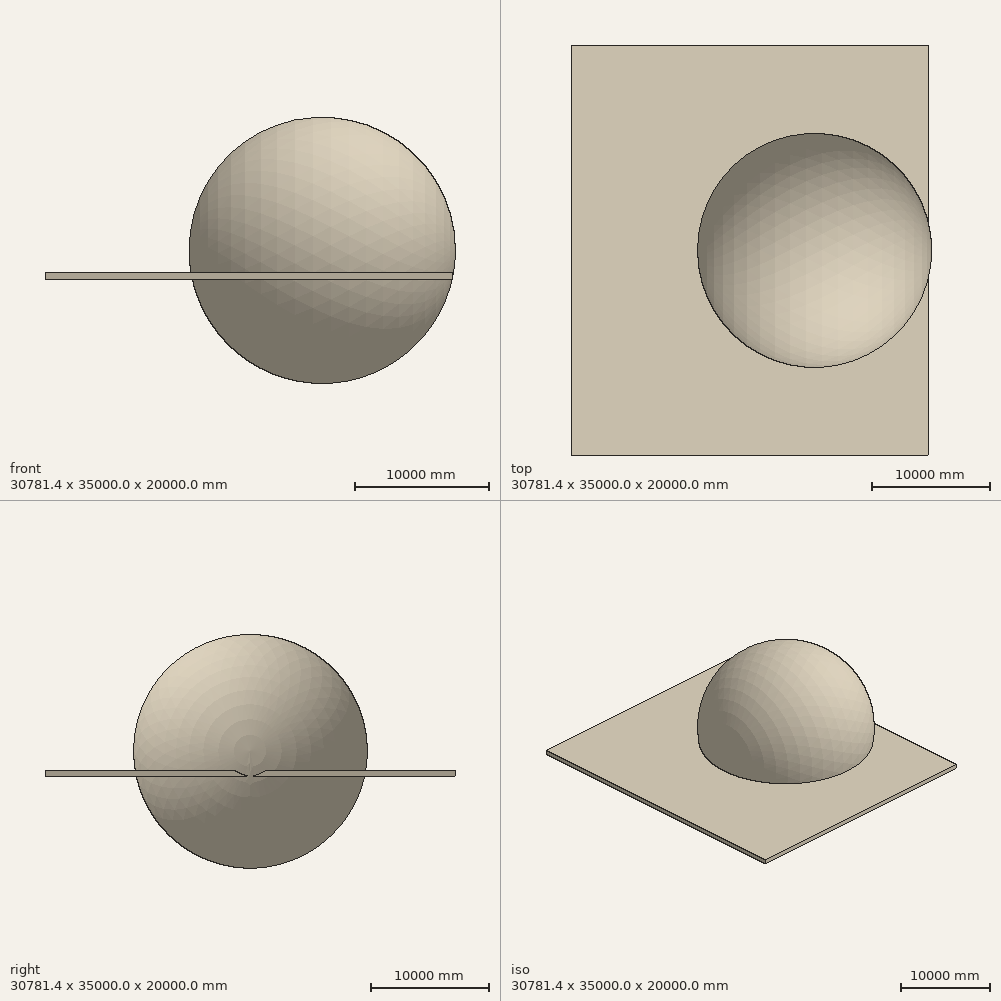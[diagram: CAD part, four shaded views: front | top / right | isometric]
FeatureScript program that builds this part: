
annotation { "Feature Type Name" : "Feature", "Feature Type Description" : "" }
export const myFeature = defineFeature(function(context is Context, id is Id, definition is map)
    precondition{}
    {
        {
            var Q0;
            Q0=qCreatedBy(makeId("Front.planeOp"),FACE);
            var sketch = newSketch(context, id + "F0", { "sketchPlane" : qUnion([Q0])});
            skLineSegment(sketch, "E0.bottom", {"start": v(0, 0) * mm, "end": v(100, 0) * mm});
            skLineSegment(sketch, "E0.top", {"start": v(0, 5000) * mm, "end": v(5000, 5000) * mm});
            skLineSegment(sketch, "E0.left", {"start": v(0, 0) * mm, "end": v(0, 5000) * mm});
            skLineSegment(sketch, "E0.right", {"start": v(5000, 0) * mm, "end": v(5000, 5000) * mm});
            skLineSegment(sketch, "E1.top", {"start": v(100, 4900) * mm, "end": v(4900, 4900) * mm});
            skLineSegment(sketch, "E1.left", {"start": v(100, 0) * mm, "end": v(100, 4900) * mm});
            skLineSegment(sketch, "E1.right", {"start": v(4900, 0) * mm, "end": v(4900, 4900) * mm});
            skLineSegment(sketch, "E2.trimOffspring", {"start": v(4900, 0) * mm, "end": v(5000, 0) * mm});
            skLineSegment(sketch, "E3.bottom", {"start": v(5500, 2156.43) * mm, "end": v(5525.4, 2156.43) * mm});
            skLineSegment(sketch, "E3.top", {"start": v(5500, 2029.43) * mm, "end": v(5525.4, 2029.43) * mm});
            skLineSegment(sketch, "E3.left", {"start": v(5500, 2156.43) * mm, "end": v(5500, 2029.43) * mm});
            skLineSegment(sketch, "E3.right", {"start": v(5525.4, 2156.43) * mm, "end": v(5525.4, 2029.43) * mm});
            skSolve(sketch);
        }
        {
            var Q0;
            Q0=makeQuery(id+"F0.imprint","IMPRINT",FACE,{"disambiguationData":[TD([[makeQuery(id+"F0.imprint","IMPRINT",EDGE,{"derivedFrom":sQuery(id+"F0.wireOp",EDGE,"E0.bottom")}),1.0]])]});
            extrude(context, id + "F1", {"entities" : qUnion([Q0]), "endBound" : BoundingType.SYMMETRIC, "depth" : 100 * mm});
        }
        {
            var Q0;
            Q0=makeQuery(id+"F0.imprint","IMPRINT",FACE,{"disambiguationData":[TD([[makeQuery(id+"F0.imprint","IMPRINT",EDGE,{"derivedFrom":sQuery(id+"F0.wireOp",EDGE,"E3.bottom")}),-1.0]])]});
            extrude(context, id + "F2", {"entities" : qUnion([Q0]), "endBound" : BoundingType.SYMMETRIC, "depth" : 25.4 * mm});
        }
        {
            var Q0;
            Q0=qCreatedBy(makeId("Top.planeOp"),FACE);
            var sketch = newSketch(context, id + "F3", { "sketchPlane" : qUnion([Q0])});
            skLineSegment(sketch, "E4.bottom", {"start": v(15268.74, 17500) * mm, "end": v(-15268.74, 17500) * mm});
            skLineSegment(sketch, "E4.top", {"start": v(15268.74, -17500) * mm, "end": v(-15268.74, -17500) * mm});
            skLineSegment(sketch, "E4.left", {"start": v(15268.74, 17500) * mm, "end": v(15268.74, -17500) * mm});
            skLineSegment(sketch, "E4.right", {"start": v(-15268.74, 17500) * mm, "end": v(-15268.74, -17500) * mm});
            skPoint(sketch, "E4.middle", {"position": v(0, 0) * mm});
            skSolve(sketch);
        }
        {
            var Q0;
            Q0 = qSketchRegion(id + "F3", true);
            extrude(context, id + "F4", {"entities" : qUnion([Q0]), "operationType" : NewBodyOperationType.ADD, "depth" : 500 * mm});
        }
        {
            var Q0;
            Q0=makeQuery(id+"F0.imprint","IMPRINT",FACE,{"disambiguationData":[TD([[makeQuery(id+"F0.imprint","IMPRINT",EDGE,{"derivedFrom":sQuery(id+"F0.wireOp",EDGE,"E3.bottom")}),-1.0]])]});
            cPlane(context, id + "F5", {"entities" : qUnion([Q0]), "cplaneType" : CPlaneType.OFFSET, "offset" : 0 * mm, "oppositeDirection" : true, "width" : 150 * mm, "height" : 150 * mm});
        }
        {
            var Q0;
            Q0=qCreatedBy(id+"F5.planeOp",FACE);
            var sketch = newSketch(context, id + "F6", { "sketchPlane" : qUnion([Q0])});
            skPoint(sketch, "E5", {"position": v(5512.7, 2156.43) * mm});
            skCircle(sketch, "E6", {"center": v(5512.7, 2156.43) * mm, "radius": 10000 * mm});
            skLineSegment(sketch, "E7", {"start": v(-4487.3, 2156.43) * mm, "end": v(15512.7, 2156.43) * mm});
            skSolve(sketch);
        }
        {
            var Q0;
            {var subQ0=sQuery(id+"F6.wireOp",EDGE,"E7");Q0=makeQuery(id+"F6.imprint","IMPRINT",FACE,{"disambiguationData":[TD([[makeQuery(id+"F6.imprint","IMPRINT",EDGE,{"derivedFrom":subQ0}),1.0]])]});}
            var Q1;
            Q1=sQuery(id+"F6.wireOp",EDGE,"E7");
            revolve(context, id + "F7", {"entities" : qUnion([Q0]), "axis" : qUnion([Q1]), "revolveType" : RevolveType.FULL});
        }
    });
